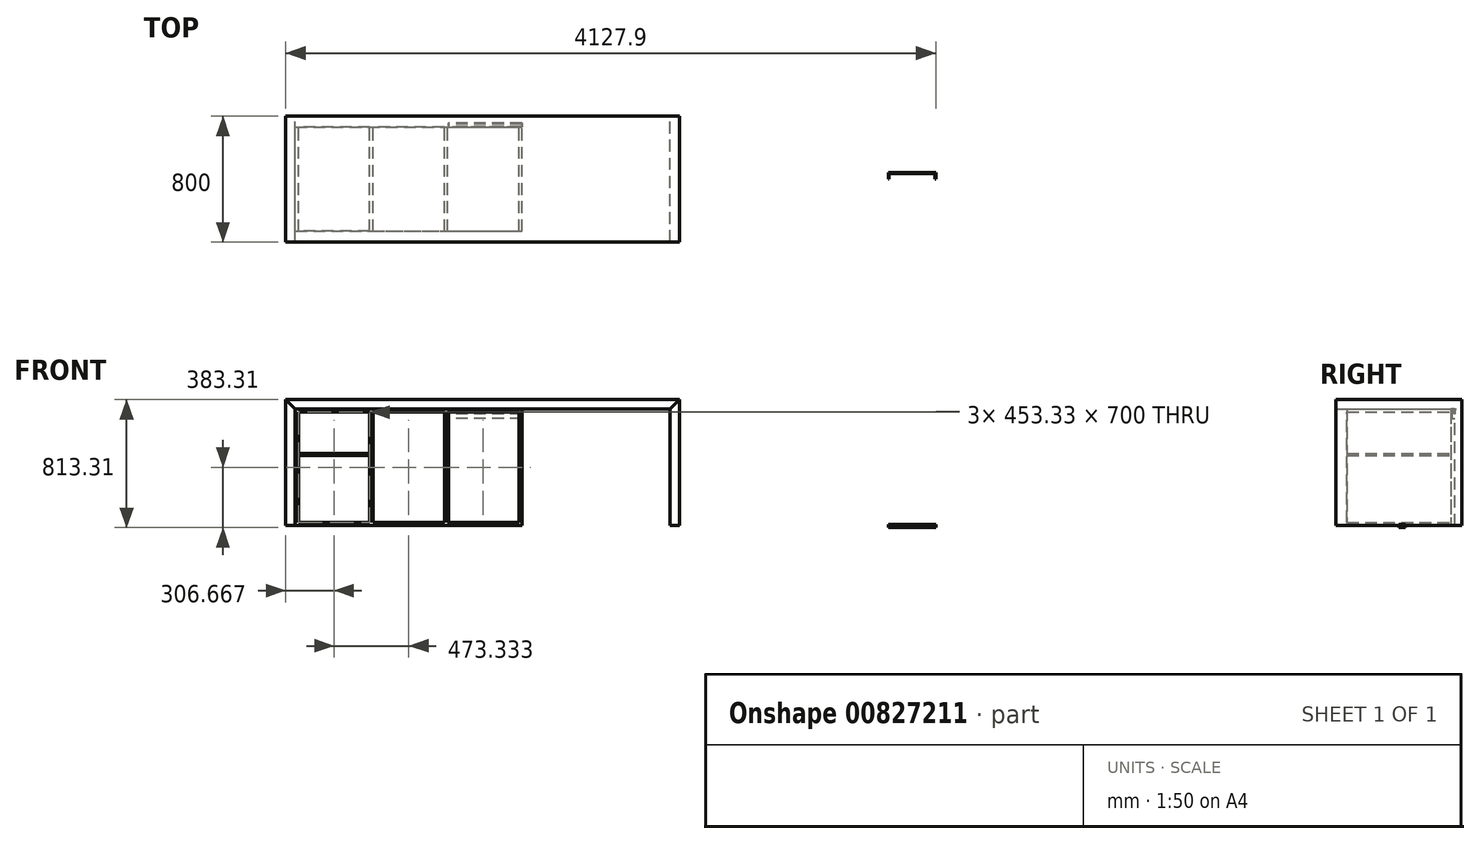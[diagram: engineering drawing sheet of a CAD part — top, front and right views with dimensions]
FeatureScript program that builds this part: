
annotation { "Feature Type Name" : "Feature", "Feature Type Description" : "" }
export const myFeature = defineFeature(function(context is Context, id is Id, definition is map)
    precondition{}
    {
        {
            var Q0;
            Q0=qCreatedBy(makeId("Front.planeOp"),FACE);
            var sketch = newSketch(context, id + "F0", { "sketchPlane" : qUnion([Q0])});
            skLineSegment(sketch, "E0", {"start": v(0, 0) * mm, "end": v(0, 740) * mm});
            skLineSegment(sketch, "E1", {"start": v(0, 740) * mm, "end": v(60, 800) * mm});
            skLineSegment(sketch, "E2", {"start": v(60, 800) * mm, "end": v(60, 0) * mm});
            skLineSegment(sketch, "E3", {"start": v(60, 0) * mm, "end": v(0, 0) * mm});
            skSolve(sketch);
        }
        {
            var Q0;
            Q0 = qSketchRegion(id + "F0", true);
            extrude(context, id + "F1", {"entities" : qUnion([Q0]), "endBound" : BoundingType.SYMMETRIC, "depth" : 800 * mm, "offsetDistance" : 25 * mm});
        }
        {
            var Q0;
            Q0=qCreatedBy(makeId("Front.planeOp"),FACE);
            var sketch = newSketch(context, id + "F2", { "sketchPlane" : qUnion([Q0])});
            skLineSegment(sketch, "E4", {"start": v(60, 800) * mm, "end": v(-2440, 800) * mm});
            skLineSegment(sketch, "E5", {"start": v(-2440, 800) * mm, "end": v(-2380, 740) * mm});
            skLineSegment(sketch, "E6", {"start": v(-2380, 740) * mm, "end": v(0, 740) * mm});
            skLineSegment(sketch, "E7", {"start": v(0, 740) * mm, "end": v(60, 800) * mm});
            skSolve(sketch);
        }
        {
            var Q0;
            Q0 = qSketchRegion(id + "F2", true);
            var Q1;
            Q1=makeQuery(id+"F1.opExtrude","CAP_FACE",FACE,{"disambiguationData":[OSD([sQuery(id+"F0.wireOp",EDGE,"E0"),sQuery(id+"F0.wireOp",EDGE,"E1"),sQuery(id+"F0.wireOp",EDGE,"E2"),sQuery(id+"F0.wireOp",EDGE,"E3")])],"isStart":false});
            extrude(context, id + "F3", {"entities" : qUnion([Q0]), "endBound" : BoundingType.SYMMETRIC, "depth" : 799 * mm, "endBoundEntityFace" : qUnion([Q1]), "offsetDistance" : 25 * mm});
        }
        {
            var Q0;
            Q0=qCreatedBy(makeId("Front.planeOp"),FACE);
            var sketch = newSketch(context, id + "F4", { "sketchPlane" : qUnion([Q0])});
            skLineSegment(sketch, "E8", {"start": v(-2440, 800) * mm, "end": v(-2440, 0) * mm});
            skLineSegment(sketch, "E9", {"start": v(-2440, 0) * mm, "end": v(-2380, 0) * mm});
            skLineSegment(sketch, "E10", {"start": v(-2380, 0) * mm, "end": v(-2380, 740) * mm});
            skLineSegment(sketch, "E11", {"start": v(-2380, 740) * mm, "end": v(-2440, 800) * mm});
            skSolve(sketch);
        }
        {
            var Q0;
            Q0 = qSketchRegion(id + "F4", true);
            extrude(context, id + "F5", {"entities" : qUnion([Q0]), "endBound" : BoundingType.SYMMETRIC, "depth" : 800 * mm, "offsetDistance" : 25 * mm});
        }
        {
            var Q0;
            Q0=qCreatedBy(makeId("Front.planeOp"),FACE);
            var sketch = newSketch(context, id + "F6", { "sketchPlane" : qUnion([Q0])});
            skLineSegment(sketch, "E12.bottom", {"start": v(-2380, 740) * mm, "end": v(-940, 740) * mm});
            skLineSegment(sketch, "E12.top", {"start": v(-2380, 0) * mm, "end": v(-940, 0) * mm});
            skLineSegment(sketch, "E12.left", {"start": v(-2380, 740) * mm, "end": v(-2380, 0) * mm});
            skLineSegment(sketch, "E12.right", {"start": v(-940, 740) * mm, "end": v(-940, 0) * mm});
            skSolve(sketch);
        }
        {
            var Q0;
            Q0 = qSketchRegion(id + "F6", true);
            extrude(context, id + "F7", {"entities" : qUnion([Q0]), "endBound" : BoundingType.SYMMETRIC, "depth" : 660 * mm, "offsetDistance" : 25 * mm});
        }
        {
            var Q0;
            Q0=makeQuery(id+"F7.opExtrude","CAP_FACE",FACE,{"disambiguationData":[OSD([sQuery(id+"F6.wireOp",EDGE,"E12.bottom"),sQuery(id+"F6.wireOp",EDGE,"E12.top"),sQuery(id+"F6.wireOp",EDGE,"E12.left"),sQuery(id+"F6.wireOp",EDGE,"E12.right")])],"isStart":true});
            var sketch = newSketch(context, id + "F8", { "sketchPlane" : qUnion([Q0])});
            skLineSegment(sketch, "E13.bottom", {"start": v(960, 720) * mm, "end": v(1413.33, 720) * mm});
            skLineSegment(sketch, "E13.top", {"start": v(960, 20) * mm, "end": v(1413.33, 20) * mm});
            skLineSegment(sketch, "E13.left", {"start": v(960, 720) * mm, "end": v(960, 20) * mm});
            skLineSegment(sketch, "E13.right", {"start": v(1413.33, 720) * mm, "end": v(1413.33, 20) * mm});
            skLineSegment(sketch, "E14.bottom", {"start": v(1433.33, 720) * mm, "end": v(1886.67, 720) * mm});
            skLineSegment(sketch, "E14.top", {"start": v(1433.33, 20) * mm, "end": v(1886.67, 20) * mm});
            skLineSegment(sketch, "E14.left", {"start": v(1433.33, 720) * mm, "end": v(1433.33, 20) * mm});
            skLineSegment(sketch, "E14.right", {"start": v(1886.67, 720) * mm, "end": v(1886.67, 20) * mm});
            skLineSegment(sketch, "E15.bottom", {"start": v(1906.67, 720) * mm, "end": v(2360, 720) * mm});
            skLineSegment(sketch, "E15.top", {"start": v(1906.67, 20) * mm, "end": v(2360, 20) * mm});
            skLineSegment(sketch, "E15.left", {"start": v(1906.67, 720) * mm, "end": v(1906.67, 20) * mm});
            skLineSegment(sketch, "E15.right", {"start": v(2360, 720) * mm, "end": v(2360, 20) * mm});
            skSolve(sketch);
        }
        {
            var Q0;
            Q0 = qSketchRegion(id + "F8", true);
            extrude(context, id + "F9", {"entities" : qUnion([Q0]), "operationType" : NewBodyOperationType.REMOVE, "endBound" : BoundingType.THROUGH_ALL, "oppositeDirection" : true, "depth" : 25 * mm, "offsetDistance" : 25 * mm});
        }
        {
            var Q0;
            Q0=makeQuery(id+"F7.opExtrude","CAP_FACE",FACE,{"disambiguationData":[OSD([sQuery(id+"F6.wireOp",EDGE,"E12.bottom"),sQuery(id+"F6.wireOp",EDGE,"E12.top"),sQuery(id+"F6.wireOp",EDGE,"E12.left"),sQuery(id+"F6.wireOp",EDGE,"E12.right")])],"isStart":true});
            var sketch = newSketch(context, id + "F10", { "sketchPlane" : qUnion([Q0])});
            skLineSegment(sketch, "E16.bottom", {"start": v(1906.67, 443.81) * mm, "end": v(2360, 443.81) * mm});
            skLineSegment(sketch, "E16.top", {"start": v(1906.67, 458.81) * mm, "end": v(2360, 458.81) * mm});
            skLineSegment(sketch, "E16.left", {"start": v(1906.67, 443.81) * mm, "end": v(1906.67, 458.81) * mm});
            skLineSegment(sketch, "E16.right", {"start": v(2360, 443.81) * mm, "end": v(2360, 458.81) * mm});
            skSolve(sketch);
        }
        {
            var Q0;
            Q0 = qSketchRegion(id + "F10", true);
            var Q1;
            Q1=makeQuery(id+"F7.opExtrude","CAP_FACE",FACE,{"disambiguationData":[OSD([sQuery(id+"F6.wireOp",EDGE,"E12.bottom"),sQuery(id+"F6.wireOp",EDGE,"E12.top"),sQuery(id+"F6.wireOp",EDGE,"E12.left"),sQuery(id+"F6.wireOp",EDGE,"E12.right")])],"isStart":false});
            extrude(context, id + "F11", {"entities" : qUnion([Q0]), "endBound" : BoundingType.UP_TO_SURFACE, "oppositeDirection" : true, "depth" : 25 * mm, "endBoundEntityFace" : qUnion([Q1]), "offsetDistance" : 25 * mm});
        }
        {
            var Q0;
            Q0=makeQuery(id+"F7.opExtrude","CAP_FACE",FACE,{"disambiguationData":[OSD([sQuery(id+"F6.wireOp",EDGE,"E12.bottom"),sQuery(id+"F6.wireOp",EDGE,"E12.top"),sQuery(id+"F6.wireOp",EDGE,"E12.left"),sQuery(id+"F6.wireOp",EDGE,"E12.right")])],"isStart":true});
            var sketch = newSketch(context, id + "F12", { "sketchPlane" : qUnion([Q0])});
            skLineSegment(sketch, "E17.bottom", {"start": v(940, 0) * mm, "end": v(1405, 0) * mm});
            skLineSegment(sketch, "E17.top", {"start": v(940, 740) * mm, "end": v(1405, 740) * mm});
            skLineSegment(sketch, "E17.left", {"start": v(940, 0) * mm, "end": v(940, 740) * mm});
            skLineSegment(sketch, "E17.right", {"start": v(1405, 0) * mm, "end": v(1405, 740) * mm});
            skSolve(sketch);
        }
        {
            var Q0;
            Q0 = qSketchRegion(id + "F12", true);
            extrude(context, id + "F13", {"entities" : qUnion([Q0]), "depth" : 25 * mm, "offsetDistance" : 25 * mm});
        }
        {
            var Q0;
            Q0=qCreatedBy(makeId("Top.planeOp"),FACE);
            var sketch = newSketch(context, id + "F14", { "sketchPlane" : qUnion([Q0])});
            skLineSegment(sketch, "E18", {"start": v(1687.03, 0) * mm, "end": v(1687.03, 40) * mm});
            skLineSegment(sketch, "E19", {"start": v(1687.03, 40) * mm, "end": v(1387.03, 40) * mm});
            skLineSegment(sketch, "E20", {"start": v(1387.03, 40) * mm, "end": v(1387.03, 0) * mm});
            skSolve(sketch);
        }
        {
            var Q0;
            Q0=qCreatedBy(makeId("Front.planeOp"),FACE);
            var sketch = newSketch(context, id + "F15", { "sketchPlane" : qUnion([Q0])});
            skLineSegment(sketch, "E21.bottom", {"start": v(1386.15, 6.7) * mm, "end": v(1391.15, 6.7) * mm});
            skLineSegment(sketch, "E21.top", {"start": v(1386.15, -13.3) * mm, "end": v(1391.15, -13.3) * mm});
            skLineSegment(sketch, "E21.left", {"start": v(1386.15, 6.7) * mm, "end": v(1386.15, -13.3) * mm});
            skLineSegment(sketch, "E21.right", {"start": v(1391.15, 6.7) * mm, "end": v(1391.15, -13.3) * mm});
            skSolve(sketch);
        }
        {
            var Q0;
            Q0=makeQuery(id+"F15.imprint","IMPRINT",FACE,{"disambiguationData":[TD([[makeQuery(id+"F15.imprint","IMPRINT",EDGE,{"derivedFrom":sQuery(id+"F15.wireOp",EDGE,"E21.bottom")}),-1.0]])]});
            var Q1;
            Q1=sQuery(id+"F14.wireOp",EDGE,"E20");
            var Q2;
            Q2=sQuery(id+"F14.wireOp",EDGE,"E19");
            var Q3;
            Q3=sQuery(id+"F14.wireOp",EDGE,"E18");
            sweep(context, id + "F16", {"profiles" : qUnion([Q0]), "path" : qUnion([Q1, Q2, Q3])});
        }
        {
            var Q0;
            Q0=makeQuery(id+"F13.opExtrude","SWEPT_FACE",FACE,{"disambiguationData":[OSD([sQuery(id+"F12.wireOp",EDGE,"E17.right")])]});
            var sketch = newSketch(context, id + "F17", { "sketchPlane" : qUnion([Q0])});
            skLineSegment(sketch, "E22", {"start": v(-355, 710) * mm, "end": v(-351, 710) * mm});
            skLineSegment(sketch, "E23", {"start": v(-351, 710) * mm, "end": v(-351, 725) * mm});
            skLineSegment(sketch, "E24", {"start": v(-351, 725) * mm, "end": v(-335, 725) * mm});
            skLineSegment(sketch, "E25", {"start": v(-335, 725) * mm, "end": v(-335, 680) * mm});
            skLineSegment(sketch, "E26", {"start": v(-335, 680) * mm, "end": v(-355, 680) * mm});
            skLineSegment(sketch, "E27", {"start": v(-355, 680) * mm, "end": v(-355, 710) * mm});
            skSolve(sketch);
        }
        {
            var Q0;
            Q0 = qSketchRegion(id + "F17", true);
            var Q1;
            Q1=makeQuery(id+"F13.opExtrude","SWEPT_FACE",FACE,{"disambiguationData":[OSD([sQuery(id+"F12.wireOp",EDGE,"E17.left")])]});
            extrude(context, id + "F18", {"entities" : qUnion([Q0]), "operationType" : NewBodyOperationType.REMOVE, "endBound" : BoundingType.UP_TO_SURFACE, "oppositeDirection" : true, "depth" : 25 * mm, "endBoundEntityFace" : qUnion([Q1]), "offsetDistance" : 25 * mm});
        }
    });
